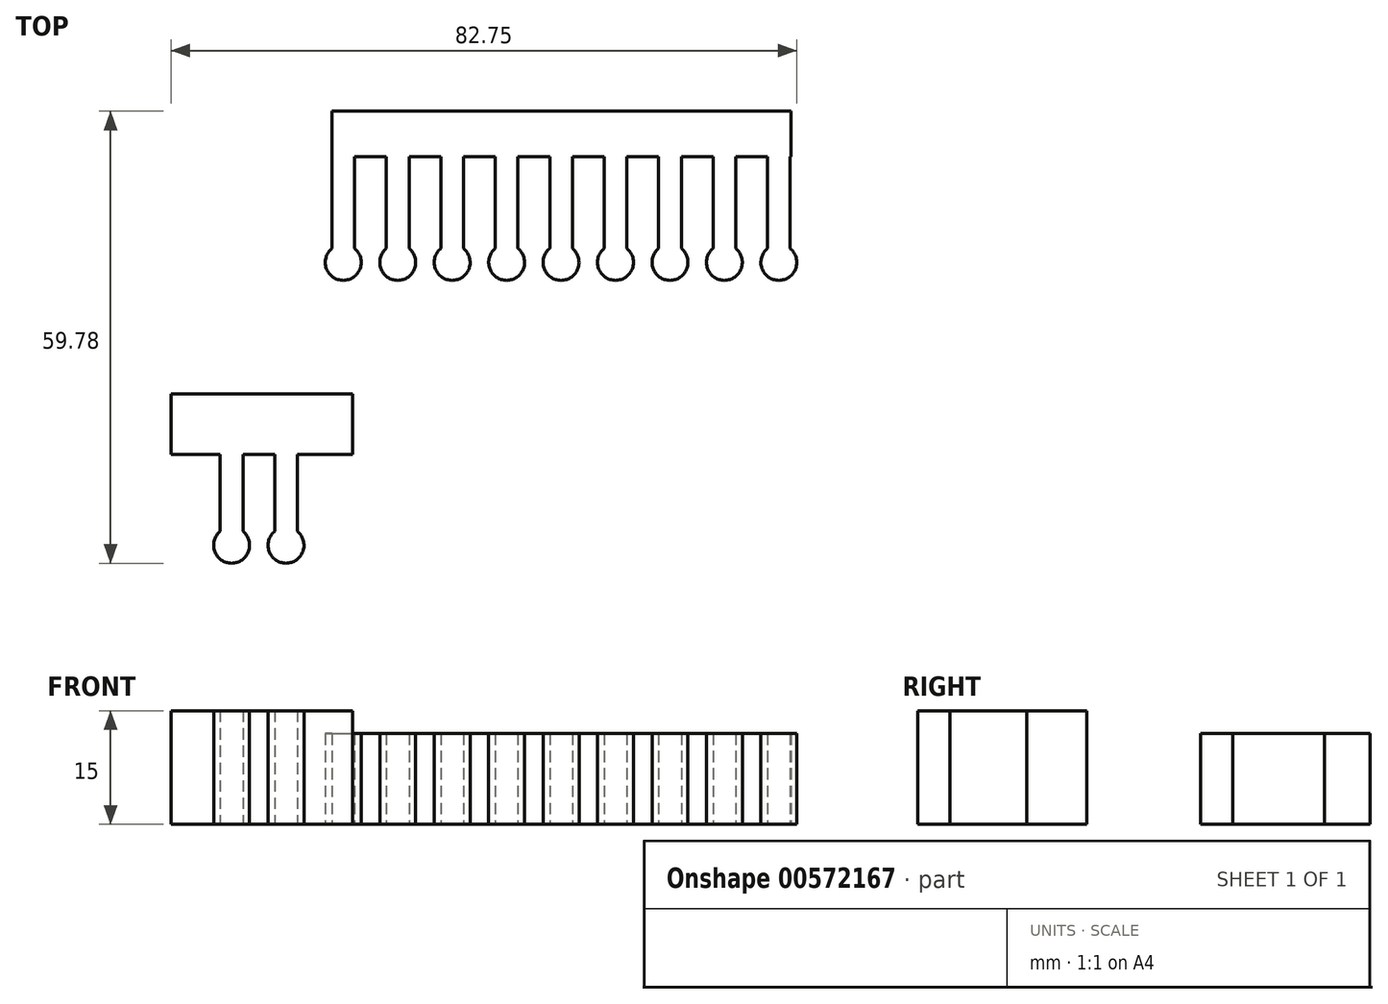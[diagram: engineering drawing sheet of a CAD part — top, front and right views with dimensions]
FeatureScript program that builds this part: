
annotation { "Feature Type Name" : "Feature", "Feature Type Description" : "" }
export const myFeature = defineFeature(function(context is Context, id is Id, definition is map)
    precondition{}
    {
        {
            var Q0;
            Q0=qCreatedBy(makeId("Top.planeOp"),FACE);
            var sketch = newSketch(context, id + "F0", { "sketchPlane" : qUnion([Q0])});
            skLineSegment(sketch, "E0.bottom", {"start": v(-61.48, 48.48) * mm, "end": v(-0.78, 48.48) * mm});
            skLineSegment(sketch, "E0.top", {"start": v(-61.48, 42.48) * mm, "end": v(-0.78, 42.48) * mm});
            skLineSegment(sketch, "E0.left", {"start": v(-61.48, 48.48) * mm, "end": v(-61.48, 42.48) * mm});
            skLineSegment(sketch, "E0.right", {"start": v(-0.78, 48.48) * mm, "end": v(-0.78, 42.48) * mm});
            skLineSegment(sketch, "E1.bottom", {"start": v(-61.48, 48.48) * mm, "end": v(-58.48, 48.48) * mm});
            skLineSegment(sketch, "E1.top", {"start": v(-61.48, 28.48) * mm, "end": v(-58.48, 28.48) * mm});
            skLineSegment(sketch, "E1.left", {"start": v(-61.48, 48.48) * mm, "end": v(-61.48, 28.48) * mm});
            skLineSegment(sketch, "E1.right", {"start": v(-58.48, 48.48) * mm, "end": v(-58.48, 28.48) * mm});
            skLineSegment(sketch, "E2.bottom", {"start": v(-54.28, 48.48) * mm, "end": v(-51.28, 48.48) * mm});
            skLineSegment(sketch, "E2.top", {"start": v(-54.28, 28.48) * mm, "end": v(-51.28, 28.48) * mm});
            skLineSegment(sketch, "E2.left", {"start": v(-54.28, 48.48) * mm, "end": v(-54.28, 28.48) * mm});
            skLineSegment(sketch, "E2.right", {"start": v(-51.28, 48.48) * mm, "end": v(-51.28, 28.48) * mm});
            skLineSegment(sketch, "E3.bottom", {"start": v(-47.08, 48.48) * mm, "end": v(-44.08, 48.48) * mm});
            skLineSegment(sketch, "E3.top", {"start": v(-47.08, 28.48) * mm, "end": v(-44.08, 28.48) * mm});
            skLineSegment(sketch, "E3.left", {"start": v(-47.08, 48.48) * mm, "end": v(-47.08, 28.48) * mm});
            skLineSegment(sketch, "E3.right", {"start": v(-44.08, 48.48) * mm, "end": v(-44.08, 28.48) * mm});
            skLineSegment(sketch, "E4.bottom", {"start": v(-39.88, 48.48) * mm, "end": v(-36.88, 48.48) * mm});
            skLineSegment(sketch, "E4.top", {"start": v(-39.88, 28.48) * mm, "end": v(-36.88, 28.48) * mm});
            skLineSegment(sketch, "E4.left", {"start": v(-39.88, 48.48) * mm, "end": v(-39.88, 28.48) * mm});
            skLineSegment(sketch, "E4.right", {"start": v(-36.88, 48.48) * mm, "end": v(-36.88, 28.48) * mm});
            skLineSegment(sketch, "E5.bottom", {"start": v(-32.68, 48.48) * mm, "end": v(-29.68, 48.48) * mm});
            skLineSegment(sketch, "E5.top", {"start": v(-32.68, 28.48) * mm, "end": v(-29.68, 28.48) * mm});
            skLineSegment(sketch, "E5.left", {"start": v(-32.68, 48.48) * mm, "end": v(-32.68, 28.48) * mm});
            skLineSegment(sketch, "E5.right", {"start": v(-29.68, 48.48) * mm, "end": v(-29.68, 28.48) * mm});
            skLineSegment(sketch, "E6.bottom", {"start": v(-25.48, 48.48) * mm, "end": v(-22.48, 48.48) * mm});
            skLineSegment(sketch, "E6.top", {"start": v(-25.48, 28.48) * mm, "end": v(-22.48, 28.48) * mm});
            skLineSegment(sketch, "E6.left", {"start": v(-25.48, 48.48) * mm, "end": v(-25.48, 28.48) * mm});
            skLineSegment(sketch, "E6.right", {"start": v(-22.48, 48.48) * mm, "end": v(-22.48, 28.48) * mm});
            skLineSegment(sketch, "E7.bottom", {"start": v(-18.28, 48.48) * mm, "end": v(-15.28, 48.48) * mm});
            skLineSegment(sketch, "E7.top", {"start": v(-18.28, 28.48) * mm, "end": v(-15.28, 28.48) * mm});
            skLineSegment(sketch, "E7.left", {"start": v(-18.28, 48.48) * mm, "end": v(-18.28, 28.48) * mm});
            skLineSegment(sketch, "E7.right", {"start": v(-15.28, 48.48) * mm, "end": v(-15.28, 28.48) * mm});
            skLineSegment(sketch, "E8.bottom", {"start": v(-11.08, 48.48) * mm, "end": v(-8.08, 48.48) * mm});
            skLineSegment(sketch, "E8.top", {"start": v(-11.08, 28.48) * mm, "end": v(-8.08, 28.48) * mm});
            skLineSegment(sketch, "E8.left", {"start": v(-11.08, 48.48) * mm, "end": v(-11.08, 28.48) * mm});
            skLineSegment(sketch, "E8.right", {"start": v(-8.08, 48.48) * mm, "end": v(-8.08, 28.48) * mm});
            skLineSegment(sketch, "E9.bottom", {"start": v(-3.88, 48.48) * mm, "end": v(-0.88, 48.48) * mm});
            skLineSegment(sketch, "E9.top", {"start": v(-3.88, 28.48) * mm, "end": v(-0.88, 28.48) * mm});
            skLineSegment(sketch, "E9.left", {"start": v(-3.88, 48.48) * mm, "end": v(-3.88, 28.48) * mm});
            skLineSegment(sketch, "E9.right", {"start": v(-0.88, 48.48) * mm, "end": v(-0.88, 28.48) * mm});
            skCircle(sketch, "E10", {"center": v(-59.98, 28.48) * mm, "radius": 2.38 * mm});
            skCircle(sketch, "E11", {"center": v(-52.78, 28.48) * mm, "radius": 2.38 * mm});
            skCircle(sketch, "E12", {"center": v(-45.58, 28.48) * mm, "radius": 2.38 * mm});
            skCircle(sketch, "E13", {"center": v(-38.38, 28.48) * mm, "radius": 2.38 * mm});
            skCircle(sketch, "E14", {"center": v(-31.18, 28.48) * mm, "radius": 2.38 * mm});
            skCircle(sketch, "E15", {"center": v(-16.78, 28.48) * mm, "radius": 2.38 * mm});
            skCircle(sketch, "E16", {"center": v(-23.98, 28.48) * mm, "radius": 2.38 * mm});
            skCircle(sketch, "E17", {"center": v(-9.58, 28.48) * mm, "radius": 2.38 * mm});
            skCircle(sketch, "E18", {"center": v(-2.38, 28.48) * mm, "radius": 2.38 * mm});
            skSolve(sketch);
        }
        {
            var Q0;
            Q0=qSketchRegion(id+"F0",true);
            extrude(context, id + "F1", {"entities" : qUnion([Q0]), "depth" : 12 * mm});
        }
        {
            var Q0;
            Q0=qCreatedBy(makeId("Top.planeOp"),FACE);
            var sketch = newSketch(context, id + "F2", { "sketchPlane" : qUnion([Q0])});
            skLineSegment(sketch, "E19.bottom", {"start": v(-76.25, 9.08) * mm, "end": v(-65.25, 9.08) * mm});
            skLineSegment(sketch, "E19.top", {"start": v(-76.25, 3.08) * mm, "end": v(-65.25, 3.08) * mm});
            skLineSegment(sketch, "E19.left", {"start": v(-76.25, 9.08) * mm, "end": v(-76.25, 3.08) * mm});
            skLineSegment(sketch, "E19.right", {"start": v(-65.25, 9.08) * mm, "end": v(-65.25, 3.08) * mm});
            skLineSegment(sketch, "E20.bottom", {"start": v(-76.25, 9.08) * mm, "end": v(-73.25, 9.08) * mm});
            skLineSegment(sketch, "E20.top", {"start": v(-76.25, -8.92) * mm, "end": v(-73.25, -8.92) * mm});
            skLineSegment(sketch, "E20.left", {"start": v(-76.25, 9.08) * mm, "end": v(-76.25, -8.92) * mm});
            skLineSegment(sketch, "E20.right", {"start": v(-73.25, 9.08) * mm, "end": v(-73.25, -8.92) * mm});
            skLineSegment(sketch, "E21.bottom", {"start": v(-69.05, 9.08) * mm, "end": v(-66.05, 9.08) * mm});
            skLineSegment(sketch, "E21.top", {"start": v(-69.05, -8.92) * mm, "end": v(-66.05, -8.92) * mm});
            skLineSegment(sketch, "E21.left", {"start": v(-69.05, 9.08) * mm, "end": v(-69.05, -8.92) * mm});
            skLineSegment(sketch, "E21.right", {"start": v(-66.05, 9.08) * mm, "end": v(-66.05, -8.92) * mm});
            skCircle(sketch, "E22", {"center": v(-74.75, -8.92) * mm, "radius": 2.38 * mm});
            skCircle(sketch, "E23", {"center": v(-67.55, -8.92) * mm, "radius": 2.38 * mm});
            skLineSegment(sketch, "E24.bottom", {"start": v(-70.75, 3.08) * mm, "end": v(-82.75, 3.08) * mm});
            skLineSegment(sketch, "E24.top", {"start": v(-70.75, 11.08) * mm, "end": v(-82.75, 11.08) * mm});
            skLineSegment(sketch, "E24.left", {"start": v(-70.75, 3.08) * mm, "end": v(-70.75, 11.08) * mm});
            skLineSegment(sketch, "E24.right", {"start": v(-82.75, 3.08) * mm, "end": v(-82.75, 11.08) * mm});
            skLineSegment(sketch, "E25.bottom", {"start": v(-70.75, 3.08) * mm, "end": v(-58.75, 3.08) * mm});
            skLineSegment(sketch, "E25.top", {"start": v(-70.75, 11.08) * mm, "end": v(-58.75, 11.08) * mm});
            skLineSegment(sketch, "E25.right", {"start": v(-58.75, 3.08) * mm, "end": v(-58.75, 11.08) * mm});
            skSolve(sketch);
        }
        {
            var Q0;
            Q0=qSketchRegion(id+"F2",true);
            extrude(context, id + "F3", {"entities" : qUnion([Q0]), "depth" : 15 * mm});
        }
    });
